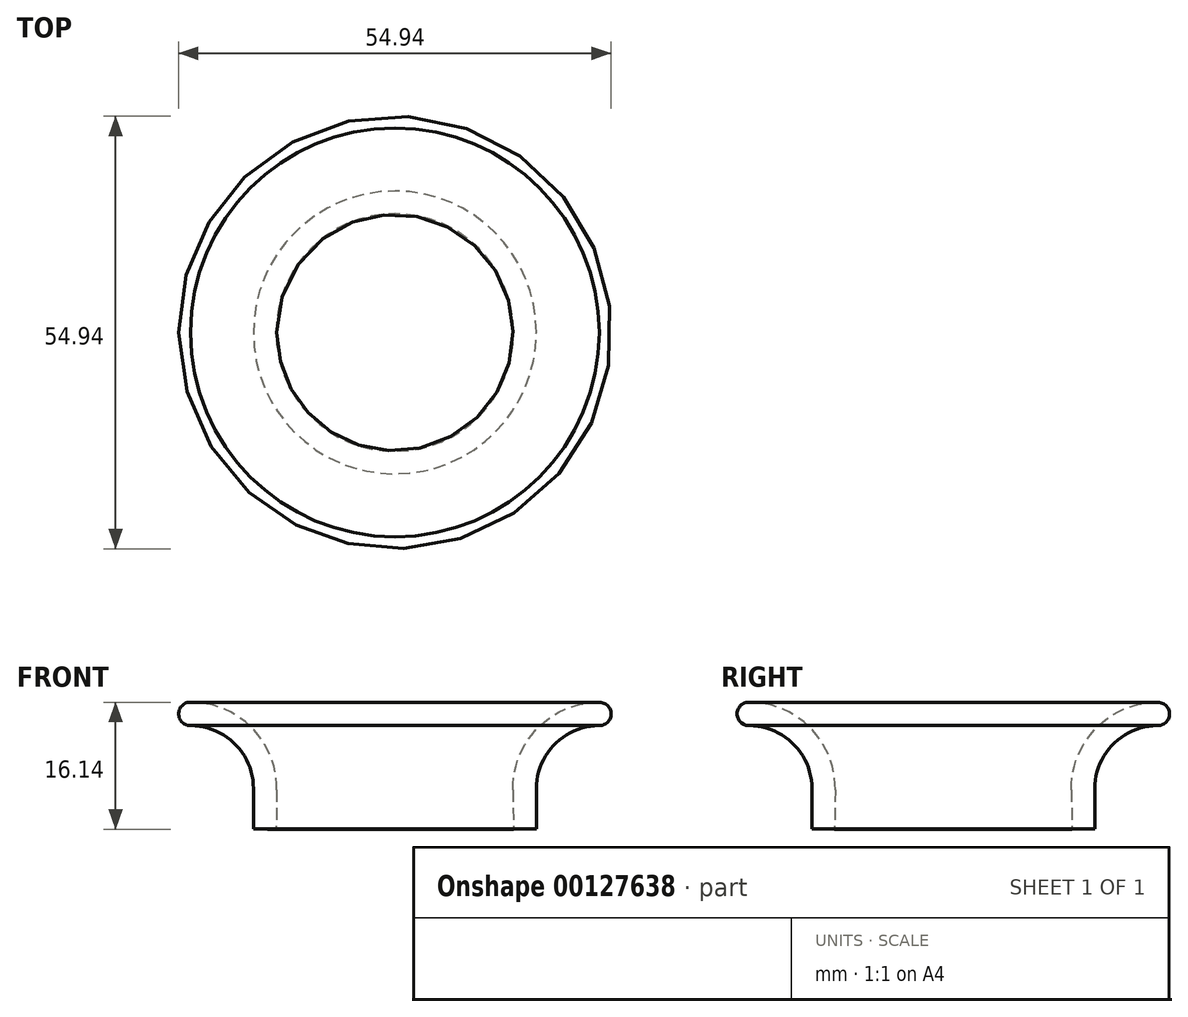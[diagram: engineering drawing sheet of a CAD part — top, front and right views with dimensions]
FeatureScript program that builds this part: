
annotation { "Feature Type Name" : "Feature", "Feature Type Description" : "" }
export const myFeature = defineFeature(function(context is Context, id is Id, definition is map)
    precondition{}
    {
        {
            var Q0;
            Q0=qCreatedBy(makeId("Front.planeOp"),FACE);
            var sketch = newSketch(context, id + "F0", { "sketchPlane" : qUnion([Q0])});
            skPoint(sketch, "E0.second.point", {"position": v(77.54, 19) * mm});
            skPoint(sketch, "E0.third.point", {"position": v(37.2, 56.24) * mm});
            skArc(sketch, "E1", {"start": v(10.97, 30.14) * mm, "mid": v(3.15, 26.86) * mm, "end": v(0, 19) * mm});
            skPoint(sketch, "E2.orphan", {"position": v(4.05, 0) * mm});
            skLineSegment(sketch, "E3", {"start": v(0, 0) * mm, "end": v(-15, 0) * mm});
            skLineSegment(sketch, "E4", {"start": v(-15, 0) * mm, "end": v(-15, 56.91) * mm});
            skArc(sketch, "E5", {"start": v(10.97, 27.17) * mm, "mid": v(5.3, 24.83) * mm, "end": v(2.97, 19.17) * mm});
            skCircle(sketch, "E6", {"center": v(9.55, 20) * mm, "radius": 0.83 * mm});
            skPoint(sketch, "E7.end.orphan", {"position": v(4.05, 10.65) * mm});
            skPoint(sketch, "E8.visualSharp", {"position": v(7.56, 0) * mm});
            skPoint(sketch, "E9.end.orphan", {"position": v(21.93, 19.17) * mm});
            skArc(sketch, "E10", {"start": v(10.97, 27.17) * mm, "mid": v(12.47, 28.65) * mm, "end": v(10.97, 30.14) * mm});
            skLineSegment(sketch, "E11", {"start": v(0, 19) * mm, "end": v(0.08, 14) * mm});
            skLineSegment(sketch, "E12", {"start": v(0.08, 14) * mm, "end": v(2.97, 14.04) * mm});
            skLineSegment(sketch, "E13", {"start": v(2.97, 14.04) * mm, "end": v(2.97, 14.17) * mm});
            skLineSegment(sketch, "E14", {"start": v(2.97, 19.17) * mm, "end": v(2.97, 15.36) * mm});
            skLineSegment(sketch, "E15", {"start": v(0.08, 14) * mm, "end": v(-15, 14) * mm});
            skLineSegment(sketch, "E16", {"start": v(2.97, 15.36) * mm, "end": v(2.97, 14.17) * mm});
            skSolve(sketch);
        }
        {
            var Q0;
            Q0=makeQuery(id+"F0.imprint","IMPRINT",FACE,{"disambiguationData":[TD([[makeQuery(id+"F0.imprint","IMPRINT",EDGE,{"derivedFrom":sQuery(id+"F0.wireOp",EDGE,"E1")}),1.0]])]});
            var Q1;
            Q1=sQuery(id+"F0.wireOp",EDGE,"E4");
            revolve(context, id + "F1", {"entities" : qUnion([Q0]), "axis" : qUnion([Q1]), "revolveType" : RevolveType.FULL});
        }
    });
